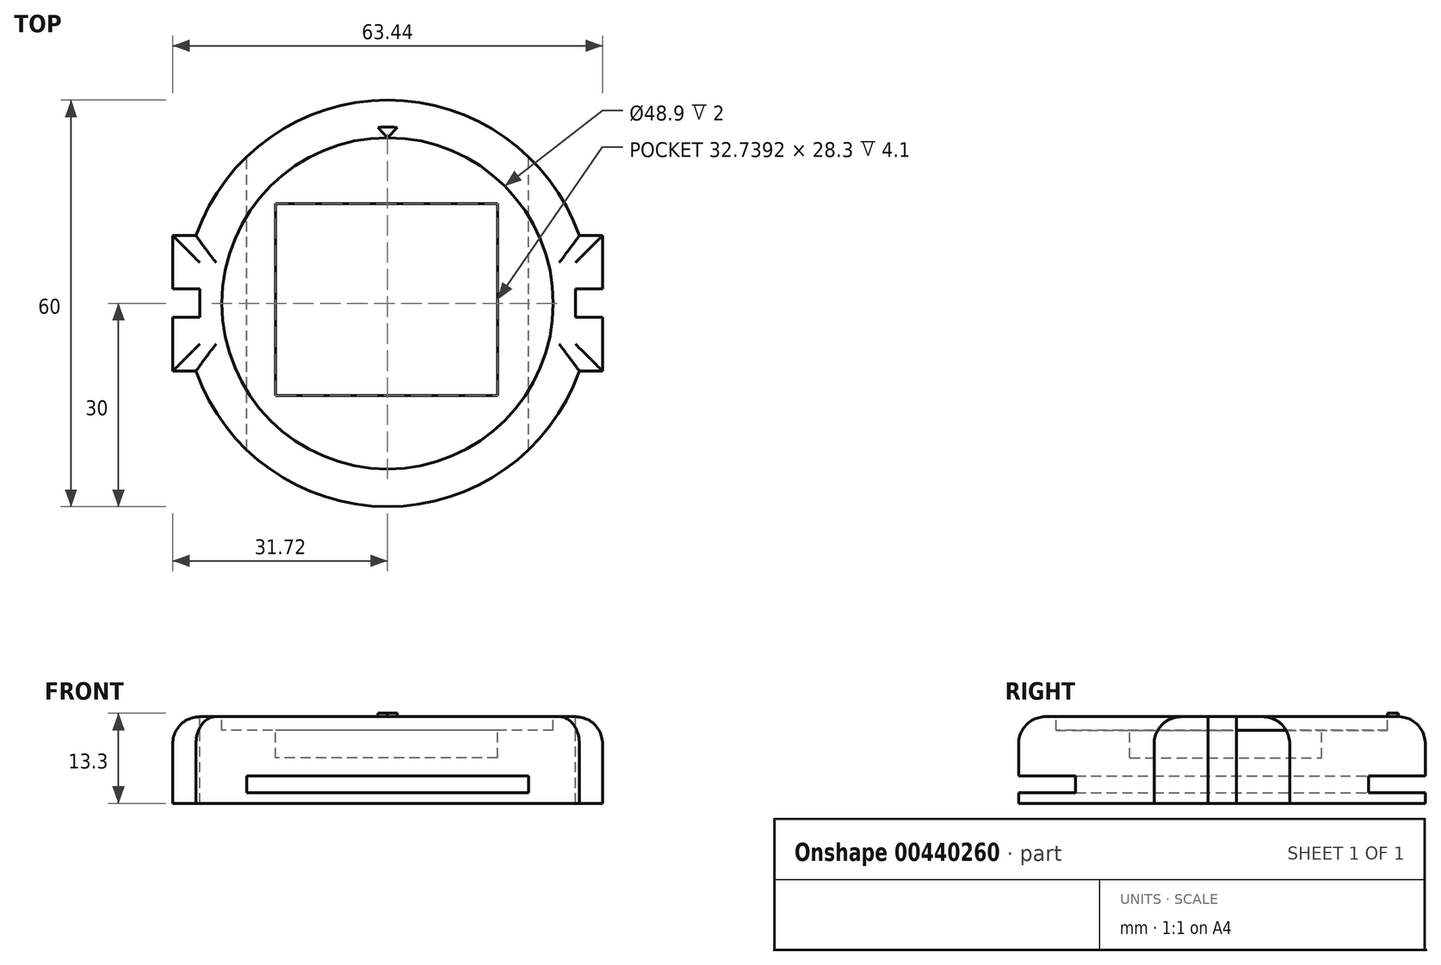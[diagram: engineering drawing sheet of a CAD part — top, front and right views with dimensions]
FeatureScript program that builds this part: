
annotation { "Feature Type Name" : "Feature", "Feature Type Description" : "" }
export const myFeature = defineFeature(function(context is Context, id is Id, definition is map)
    precondition{}
    {
        {
            var Q0;
            Q0=qCreatedBy(makeId("Top.planeOp"),FACE);
            var sketch = newSketch(context, id + "F0", { "sketchPlane" : qUnion([Q0])});
            skArc(sketch, "E0", {"start": v(0, 30) * mm, "mid": v(-17.32, 24.5) * mm, "end": v(-28.28, 10) * mm});
            skLineSegment(sketch, "E1.bottom", {"start": v(-28.28, -10) * mm, "end": v(-31.72, -10) * mm});
            skLineSegment(sketch, "E1.top", {"start": v(-28.28, 10) * mm, "end": v(-31.72, 10) * mm});
            skLineSegment(sketch, "E1.right", {"start": v(-31.72, -10) * mm, "end": v(-31.72, 10) * mm});
            skPoint(sketch, "E1.middle", {"position": v(-30, 0) * mm});
            skArc(sketch, "E2.trimOffspring", {"start": v(-28.28, -10) * mm, "mid": v(-17.32, -24.5) * mm, "end": v(0, -30) * mm});
            skLineSegment(sketch, "E3.MirrorCS", {"start": v(28.28, -10) * mm, "end": v(31.72, -10) * mm});
            skPoint(sketch, "E4.MirrorP", {"position": v(30, 0) * mm});
            skLineSegment(sketch, "E5.MirrorCS", {"start": v(28.28, 10) * mm, "end": v(31.72, 10) * mm});
            skLineSegment(sketch, "E6.MirrorCS", {"start": v(31.72, -10) * mm, "end": v(31.72, 10) * mm});
            skArc(sketch, "E7.MirrorCS", {"start": v(0, 30) * mm, "mid": v(17.32, 24.5) * mm, "end": v(28.28, 10) * mm});
            skArc(sketch, "E8.MirrorCS", {"start": v(28.28, -10) * mm, "mid": v(17.32, -24.5) * mm, "end": v(0, -30) * mm});
            skSolve(sketch);
        }
        {
            var Q0;
            Q0=makeQuery(id+"F0.imprint","IMPRINT",FACE,{"disambiguationData":[TD([[makeQuery(id+"F0.imprint","IMPRINT",EDGE,{"derivedFrom":sQuery(id+"F0.wireOp",EDGE,"E0")}),1.0]])]});
            extrude(context, id + "F1", {"entities" : qUnion([Q0]), "depth" : 10 * mm});
        }
        {
            var Q0;
            Q0=makeQuery(id+"F1.opExtrude","CAP_FACE",FACE,{"disambiguationData":[OSD([sQuery(id+"F0.wireOp",EDGE,"E0"),sQuery(id+"F0.wireOp",EDGE,"E1.bottom"),sQuery(id+"F0.wireOp",EDGE,"E1.top"),sQuery(id+"F0.wireOp",EDGE,"E1.right"),sQuery(id+"F0.wireOp",EDGE,"E2.trimOffspring"),sQuery(id+"F0.wireOp",EDGE,"E3.MirrorCS"),sQuery(id+"F0.wireOp",EDGE,"E5.MirrorCS"),sQuery(id+"F0.wireOp",EDGE,"E6.MirrorCS"),sQuery(id+"F0.wireOp",EDGE,"E7.MirrorCS"),sQuery(id+"F0.wireOp",EDGE,"E8.MirrorCS")])],"isStart":false});
            var sketch = newSketch(context, id + "F2", { "sketchPlane" : qUnion([Q0])});
            skCircle(sketch, "E9", {"center": v(0, 0) * mm, "radius": 24.45 * mm});
            skSolve(sketch);
        }
        {
            var Q0;
            Q0=makeQuery(id+"F1.opExtrude","CAP_FACE",FACE,{"disambiguationData":[OSD([sQuery(id+"F0.wireOp",EDGE,"E0"),sQuery(id+"F0.wireOp",EDGE,"E1.bottom"),sQuery(id+"F0.wireOp",EDGE,"E1.top"),sQuery(id+"F0.wireOp",EDGE,"E1.right"),sQuery(id+"F0.wireOp",EDGE,"E2.trimOffspring"),sQuery(id+"F0.wireOp",EDGE,"E3.MirrorCS"),sQuery(id+"F0.wireOp",EDGE,"E5.MirrorCS"),sQuery(id+"F0.wireOp",EDGE,"E6.MirrorCS"),sQuery(id+"F0.wireOp",EDGE,"E7.MirrorCS"),sQuery(id+"F0.wireOp",EDGE,"E8.MirrorCS")])],"isStart":false});
            fillet(context, id + "F3", {"entities" : qUnion([Q0]), "radius" : 4 * mm, "tangentPropagation" : true, "allowEdgeOverflow" : false});
        }
        {
            var Q0;
            Q0=makeQuery(id+"F2.imprint","IMPRINT",FACE,{"disambiguationData":[TD([[makeQuery(id+"F2.imprint","IMPRINT",EDGE,{"derivedFrom":sQuery(id+"F2.wireOp",EDGE,"E9")}),1.0]])]});
            extrude(context, id + "F4", {"entities" : qUnion([Q0]), "operationType" : NewBodyOperationType.REMOVE, "oppositeDirection" : true, "depth" : 2 * mm});
        }
        {
            var Q0;
            Q0=makeQuery(id+"F4.boolean.opBoolean","COPY",FACE,{"derivedFrom":makeQuery(id+"F4.opExtrude","CAP_FACE",FACE,{"disambiguationData":[OSD([sQuery(id+"F2.wireOp",EDGE,"E9")])],"isStart":false})});
            var sketch = newSketch(context, id + "F5", { "sketchPlane" : qUnion([Q0])});
            skLineSegment(sketch, "E10.bottom", {"start": v(16.23, -13.59) * mm, "end": v(-16.5, -13.59) * mm});
            skLineSegment(sketch, "E10.top", {"start": v(16.23, 14.71) * mm, "end": v(-16.5, 14.71) * mm});
            skLineSegment(sketch, "E10.left", {"start": v(16.23, -13.59) * mm, "end": v(16.23, 14.71) * mm});
            skLineSegment(sketch, "E10.right", {"start": v(-16.5, -13.59) * mm, "end": v(-16.5, 14.71) * mm});
            skPoint(sketch, "E10.middle", {"position": v(-0.14, 0.56) * mm});
            skSolve(sketch);
        }
        {
            var Q0;
            Q0=makeQuery(id+"F1.opExtrude","CAP_FACE",FACE,{"disambiguationData":[OSD([sQuery(id+"F0.wireOp",EDGE,"E0"),sQuery(id+"F0.wireOp",EDGE,"E1.bottom"),sQuery(id+"F0.wireOp",EDGE,"E1.top"),sQuery(id+"F0.wireOp",EDGE,"E1.right"),sQuery(id+"F0.wireOp",EDGE,"E2.trimOffspring"),sQuery(id+"F0.wireOp",EDGE,"E3.MirrorCS"),sQuery(id+"F0.wireOp",EDGE,"E5.MirrorCS"),sQuery(id+"F0.wireOp",EDGE,"E6.MirrorCS"),sQuery(id+"F0.wireOp",EDGE,"E7.MirrorCS"),sQuery(id+"F0.wireOp",EDGE,"E8.MirrorCS")])],"isStart":false});
            var sketch = newSketch(context, id + "F6", { "sketchPlane" : qUnion([Q0])});
            skLineSegment(sketch, "E11", {"start": v(0, 24.45) * mm, "end": v(1.43, 25.96) * mm});
            skLineSegment(sketch, "E12.MirrorCS", {"start": v(0, 24.45) * mm, "end": v(-1.43, 25.96) * mm});
            skSolve(sketch);
        }
        {
            var Q0;
            {var subQ0=sQuery(id+"F6.wireOp",EDGE,"E11");Q0=makeQuery(id+"F6.imprint","IMPRINT",FACE,{"disambiguationData":[TD([[makeQuery(id+"F6.imprint","IMPRINT",EDGE,{"derivedFrom":subQ0}),1.0]])]});}
            extrude(context, id + "F7", {"entities" : qUnion([Q0]), "operationType" : NewBodyOperationType.ADD, "depth" : .5 * mm});
        }
        {
            var Q0;
            Q0=makeQuery(id+"F1.opExtrude","CAP_FACE",FACE,{"disambiguationData":[OSD([sQuery(id+"F0.wireOp",EDGE,"E0"),sQuery(id+"F0.wireOp",EDGE,"E1.bottom"),sQuery(id+"F0.wireOp",EDGE,"E1.top"),sQuery(id+"F0.wireOp",EDGE,"E1.right"),sQuery(id+"F0.wireOp",EDGE,"E2.trimOffspring"),sQuery(id+"F0.wireOp",EDGE,"E3.MirrorCS"),sQuery(id+"F0.wireOp",EDGE,"E5.MirrorCS"),sQuery(id+"F0.wireOp",EDGE,"E6.MirrorCS"),sQuery(id+"F0.wireOp",EDGE,"E7.MirrorCS"),sQuery(id+"F0.wireOp",EDGE,"E8.MirrorCS")])],"isStart":false});
            var sketch = newSketch(context, id + "F8", { "sketchPlane" : qUnion([Q0])});
            skLineSegment(sketch, "E13.bottom", {"start": v(-27.72, -2.03) * mm, "end": v(-33.75, -2.03) * mm});
            skLineSegment(sketch, "E13.top", {"start": v(-27.72, 2.17) * mm, "end": v(-33.75, 2.17) * mm});
            skLineSegment(sketch, "E13.left", {"start": v(-27.72, -2.03) * mm, "end": v(-27.72, 2.17) * mm});
            skLineSegment(sketch, "E13.right", {"start": v(-33.75, -2.03) * mm, "end": v(-33.75, 2.17) * mm});
            skLineSegment(sketch, "E14.MirrorCS", {"start": v(33.75, -2.03) * mm, "end": v(33.75, 2.17) * mm});
            skLineSegment(sketch, "E15.MirrorCS", {"start": v(27.72, 2.17) * mm, "end": v(33.75, 2.17) * mm});
            skLineSegment(sketch, "E16.MirrorCS", {"start": v(27.72, -2.03) * mm, "end": v(27.72, 2.17) * mm});
            skLineSegment(sketch, "E17.MirrorCS", {"start": v(27.72, -2.03) * mm, "end": v(33.75, -2.03) * mm});
            skSolve(sketch);
        }
        {
            var Q0;
            Q0 = qSketchRegion(id + "F8", true);
            extrude(context, id + "F9", {"entities" : qUnion([Q0]), "operationType" : NewBodyOperationType.REMOVE, "oppositeDirection" : true, "depth" : 25 * mm});
        }
        {
            var Q0;
            Q0=makeQuery(id+"F5.imprint","IMPRINT",FACE,{"disambiguationData":[TD([[makeQuery(id+"F5.imprint","IMPRINT",EDGE,{"derivedFrom":sQuery(id+"F5.wireOp",EDGE,"E10.bottom")}),-1.0]])]});
            extrude(context, id + "F10", {"entities" : qUnion([Q0]), "operationType" : NewBodyOperationType.REMOVE, "oppositeDirection" : true, "depth" : 4.1 * mm});
        }
        {
            var Q0;
            Q0=makeQuery(id+"F1.opExtrude","CAP_FACE",FACE,{"disambiguationData":[OSD([sQuery(id+"F0.wireOp",EDGE,"E0"),sQuery(id+"F0.wireOp",EDGE,"E1.bottom"),sQuery(id+"F0.wireOp",EDGE,"E1.top"),sQuery(id+"F0.wireOp",EDGE,"E1.right"),sQuery(id+"F0.wireOp",EDGE,"E2.trimOffspring"),sQuery(id+"F0.wireOp",EDGE,"E3.MirrorCS"),sQuery(id+"F0.wireOp",EDGE,"E5.MirrorCS"),sQuery(id+"F0.wireOp",EDGE,"E6.MirrorCS"),sQuery(id+"F0.wireOp",EDGE,"E7.MirrorCS"),sQuery(id+"F0.wireOp",EDGE,"E8.MirrorCS")])],"isStart":true});
            extrude(context, id + "F11", {"entities" : qUnion([Q0]), "operationType" : NewBodyOperationType.ADD, "depth" : 2.8 * mm});
        }
        {
            var Q0;
            Q0=qCreatedBy(makeId("Front.planeOp"),FACE);
            var sketch = newSketch(context, id + "F12", { "sketchPlane" : qUnion([Q0])});
            skLineSegment(sketch, "E18.bottom", {"start": v(20.81, -1.25) * mm, "end": v(-20.81, -1.25) * mm});
            skLineSegment(sketch, "E18.top", {"start": v(20.81, 1.25) * mm, "end": v(-20.81, 1.25) * mm});
            skLineSegment(sketch, "E18.left", {"start": v(20.81, -1.25) * mm, "end": v(20.81, 1.25) * mm});
            skLineSegment(sketch, "E18.right", {"start": v(-20.81, -1.25) * mm, "end": v(-20.81, 1.25) * mm});
            skPoint(sketch, "E18.middle", {"position": v(0, 0) * mm});
            skSolve(sketch);
        }
        {
            var Q0;
            Q0 = qSketchRegion(id + "F12", true);
            var Q1;
            Q1=sQuery(id+"F12.wireOp",EDGE,"E18.right");
            var Q2;
            Q2=sQuery(id+"F12.wireOp",EDGE,"E18.top");
            var Q3;
            Q3=sQuery(id+"F12.wireOp",EDGE,"E18.bottom");
            var Q4;
            Q4=sQuery(id+"F12.wireOp",EDGE,"E18.left");
            extrude(context, id + "F13", {"entities" : qUnion([Q0]), "operationType" : NewBodyOperationType.REMOVE, "surfaceEntities" : qUnion([Q1, Q2, Q3, Q4]), "endBound" : BoundingType.SYMMETRIC, "depth" : 77.7 * mm});
        }
    });
